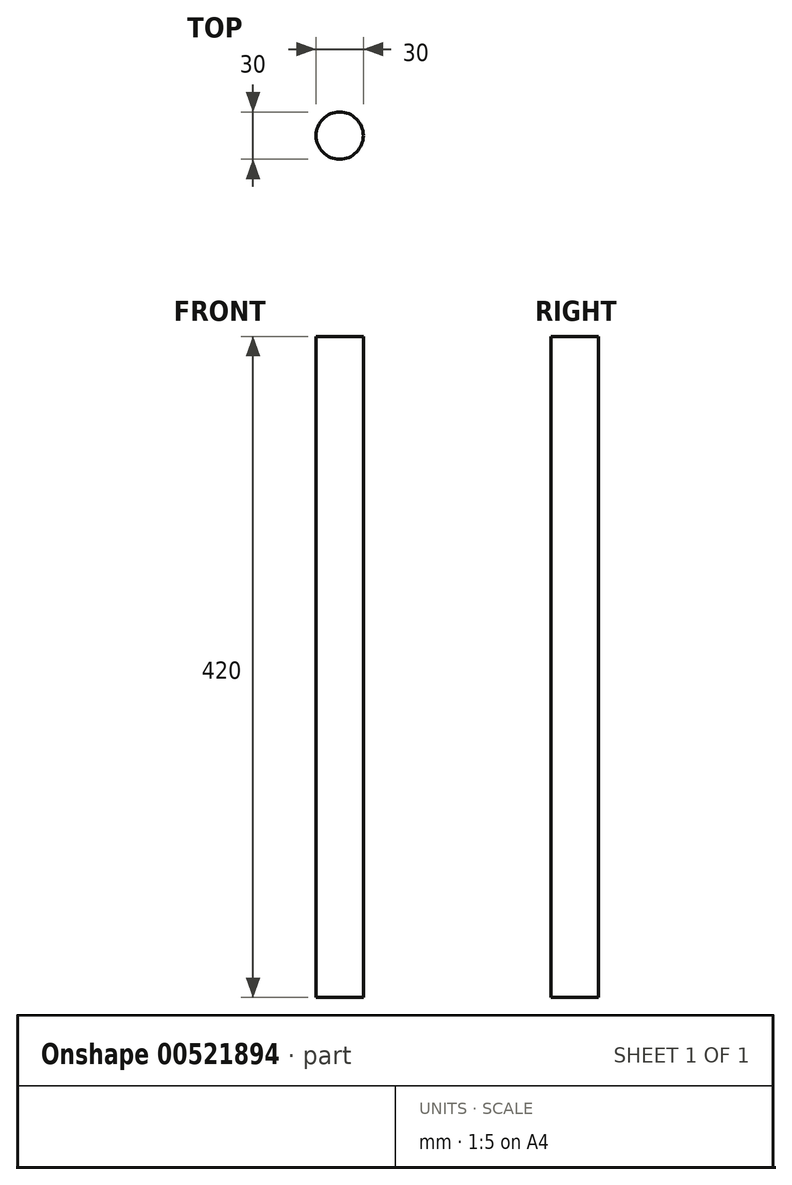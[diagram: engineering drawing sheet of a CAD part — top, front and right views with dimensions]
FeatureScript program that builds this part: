
annotation { "Feature Type Name" : "Feature", "Feature Type Description" : "" }
export const myFeature = defineFeature(function(context is Context, id is Id, definition is map)
    precondition{}
    {
        {
            var Q0;
            Q0=qCreatedBy(makeId("Top.planeOp"),FACE);
            var sketch = newSketch(context, id + "F0", { "sketchPlane" : qUnion([Q0])});
            skCircle(sketch, "E0", {"center": v(0, 0) * mm, "radius": 15 * mm});
            skSolve(sketch);
        }
        {
            var Q0;
            Q0=qSketchRegion(id+"F0",true);
            extrude(context, id + "F1", {"entities" : qUnion([Q0]), "depth" : 420 * mm, "offsetDistance" : 25 * mm});
        }
    });
